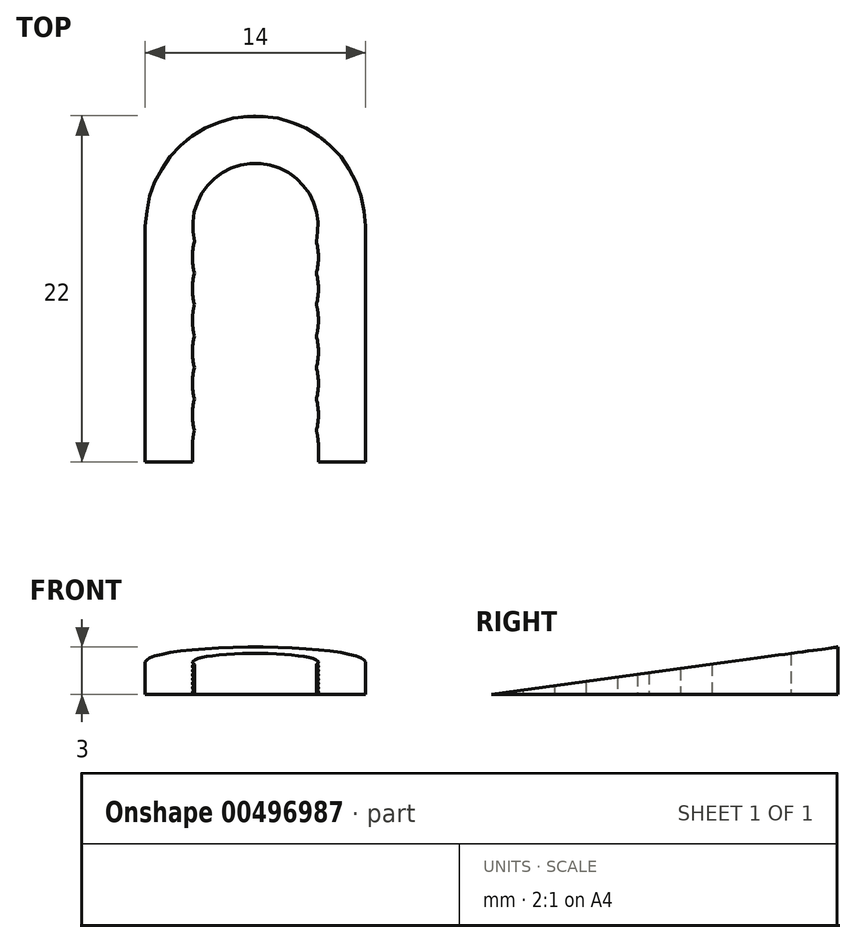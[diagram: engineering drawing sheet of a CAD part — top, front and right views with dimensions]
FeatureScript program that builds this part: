
annotation { "Feature Type Name" : "Feature", "Feature Type Description" : "" }
export const myFeature = defineFeature(function(context is Context, id is Id, definition is map)
    precondition{}
    {
        {
            var Q0;
            Q0=qCreatedBy(makeId("Top.planeOp"),FACE);
            var sketch = newSketch(context, id + "F0", { "sketchPlane" : qUnion([Q0])});
            skCircle(sketch, "E0", {"center": v(0, 0) * mm, "radius": 4 * mm});
            skCircle(sketch, "E1", {"center": v(0, 0) * mm, "radius": 7 * mm});
            skLineSegment(sketch, "E2.bottom", {"start": v(-7, 0) * mm, "end": v(7, 0) * mm});
            skLineSegment(sketch, "E2.top", {"start": v(-7, -15) * mm, "end": v(7, -15) * mm});
            skLineSegment(sketch, "E2.left", {"start": v(-7, 0) * mm, "end": v(-7, -15) * mm});
            skLineSegment(sketch, "E2.right", {"start": v(7, 0) * mm, "end": v(7, -15) * mm});
            skLineSegment(sketch, "E3.bottom", {"start": v(-4, 0) * mm, "end": v(4, 0) * mm});
            skLineSegment(sketch, "E3.top", {"start": v(-4, -15) * mm, "end": v(4, -15) * mm});
            skLineSegment(sketch, "E3.left", {"start": v(-4, 0) * mm, "end": v(-4, -15) * mm});
            skLineSegment(sketch, "E3.right", {"start": v(4, 0) * mm, "end": v(4, -15) * mm});
            skLineSegment(sketch, "E4", {"start": v(0, 0) * mm, "end": v(0, -15) * mm, "construction": true});
            skCircle(sketch, "E5.1.0.0", {"center": v(0, -2) * mm, "radius": 4 * mm});
            skCircle(sketch, "E5.2.0.0", {"center": v(0, -4) * mm, "radius": 4 * mm});
            skCircle(sketch, "E5.3.0.0", {"center": v(0, -6) * mm, "radius": 4 * mm});
            skCircle(sketch, "E5.4.0.0", {"center": v(0, -8) * mm, "radius": 4 * mm});
            skCircle(sketch, "E5.5.0.0", {"center": v(0, -10) * mm, "radius": 4 * mm});
            skCircle(sketch, "E5.6.0.0", {"center": v(0, -12) * mm, "radius": 4 * mm});
            skCircle(sketch, "E5.7.0.0", {"center": v(0, -14) * mm, "radius": 4 * mm});
            skLineSegment(sketch, "E5.direction1", {"start": v(0, 0) * mm, "end": v(0, -2) * mm, "construction": true});
            skSolve(sketch);
        }
        {
            var Q0;
            {var subQ4=sQuery(id+"F0.wireOp",EDGE,"E2.left");Q0=makeQuery(id+"F0.imprint","IMPRINT",FACE,{"disambiguationData":[TD([[makeQuery(id+"F0.imprint","IMPRINT",EDGE,{"derivedFrom":subQ4}),1.0]])]});}
            var Q1;
            {var subQ0=sQuery(id+"F0.wireOp",EDGE,"E3.left");var subQ1=makeQuery(id+"F0.imprint","INTERSECT",VERTEX,{"derivedFrom":[subQ0,sQuery(id+"F0.wireOp",EDGE,"E5.1.0.0")]});Q1=makeQuery(id+"F0.imprint","IMPRINT",FACE,{"disambiguationData":[TD([[makeQuery(id+"F0.imprint","IMPRINT",EDGE,{"disambiguationData":[TD([[subQ1,-1.0]])],"derivedFrom":subQ0}),-1.0]])]});}
            var Q2;
            {var subQ1=sQuery(id+"F0.wireOp",EDGE,"E2.bottom");var subQ5=sQuery(id+"F0.wireOp",EDGE,"E1");var subQ6=makeQuery(id+"F0.imprint","INTERSECT",VERTEX,{"derivedFrom":[subQ5,subQ1,sQuery(id+"F0.wireOp",EDGE,"E2.left")]});Q2=makeQuery(id+"F0.imprint","IMPRINT",FACE,{"disambiguationData":[TD([[makeQuery(id+"F0.imprint","IMPRINT",EDGE,{"disambiguationData":[TD([[subQ6,1.0]])],"derivedFrom":subQ5}),1.0]])]});}
            var Q3;
            {var subQ0=sQuery(id+"F0.wireOp",EDGE,"E3.right");var subQ1=makeQuery(id+"F0.imprint","INTERSECT",VERTEX,{"derivedFrom":[subQ0,sQuery(id+"F0.wireOp",EDGE,"E5.1.0.0")]});Q3=makeQuery(id+"F0.imprint","IMPRINT",FACE,{"disambiguationData":[TD([[makeQuery(id+"F0.imprint","IMPRINT",EDGE,{"disambiguationData":[TD([[subQ1,-1.0]])],"derivedFrom":subQ0}),1.0]])]});}
            var Q4;
            {var subQ4=sQuery(id+"F0.wireOp",EDGE,"E2.right");Q4=makeQuery(id+"F0.imprint","IMPRINT",FACE,{"disambiguationData":[TD([[makeQuery(id+"F0.imprint","IMPRINT",EDGE,{"derivedFrom":subQ4}),-1.0]])]});}
            var Q5;
            {var subQ1=sQuery(id+"F0.wireOp",EDGE,"E0");var subQ3=sQuery(id+"F0.wireOp",EDGE,"E5.1.0.0");var subQ4=makeQuery(id+"F0.imprint","INTERSECT",VERTEX,{"disambiguationData":[OD(0.0)],"derivedFrom":[subQ1,subQ3]});Q5=makeQuery(id+"F0.imprint","IMPRINT",FACE,{"disambiguationData":[TD([[makeQuery(id+"F0.imprint","IMPRINT",EDGE,{"disambiguationData":[TD([[subQ4,-1.0]])],"derivedFrom":subQ3}),-1.0]])]});}
            var Q6;
            {var subQ0=sQuery(id+"F0.wireOp",EDGE,"E5.1.0.0");var subQ1=sQuery(id+"F0.wireOp",EDGE,"E3.left");var subQ2=makeQuery(id+"F0.imprint","INTERSECT",VERTEX,{"derivedFrom":[subQ1,subQ0]});Q6=makeQuery(id+"F0.imprint","IMPRINT",FACE,{"disambiguationData":[TD([[makeQuery(id+"F0.imprint","IMPRINT",EDGE,{"disambiguationData":[TD([[subQ2,-1.0]])],"derivedFrom":subQ1}),1.0]])]});}
            var Q7;
            {var subQ0=sQuery(id+"F0.wireOp",EDGE,"E3.left");var subQ1=sQuery(id+"F0.wireOp",EDGE,"E1");var subQ2=makeQuery(id+"F0.imprint","INTERSECT",VERTEX,{"derivedFrom":[subQ1,subQ0]});Q7=makeQuery(id+"F0.imprint","IMPRINT",FACE,{"disambiguationData":[TD([[makeQuery(id+"F0.imprint","IMPRINT",EDGE,{"disambiguationData":[TD([[subQ2,-1.0]])],"derivedFrom":subQ1}),1.0]])]});}
            var Q8;
            {var subQ0=sQuery(id+"F0.wireOp",EDGE,"E5.3.0.0");var subQ1=sQuery(id+"F0.wireOp",EDGE,"E3.left");var subQ2=makeQuery(id+"F0.imprint","INTERSECT",VERTEX,{"derivedFrom":[subQ1,subQ0]});Q8=makeQuery(id+"F0.imprint","IMPRINT",FACE,{"disambiguationData":[TD([[makeQuery(id+"F0.imprint","IMPRINT",EDGE,{"disambiguationData":[TD([[subQ2,-1.0]])],"derivedFrom":subQ1}),1.0]])]});}
            var Q9;
            {var subQ0=sQuery(id+"F0.wireOp",EDGE,"E5.4.0.0");var subQ1=sQuery(id+"F0.wireOp",EDGE,"E3.left");var subQ2=makeQuery(id+"F0.imprint","INTERSECT",VERTEX,{"derivedFrom":[subQ1,subQ0]});Q9=makeQuery(id+"F0.imprint","IMPRINT",FACE,{"disambiguationData":[TD([[makeQuery(id+"F0.imprint","IMPRINT",EDGE,{"disambiguationData":[TD([[subQ2,-1.0]])],"derivedFrom":subQ1}),1.0]])]});}
            var Q10;
            {var subQ0=sQuery(id+"F0.wireOp",EDGE,"E5.5.0.0");var subQ1=sQuery(id+"F0.wireOp",EDGE,"E3.left");var subQ2=makeQuery(id+"F0.imprint","INTERSECT",VERTEX,{"derivedFrom":[subQ1,subQ0]});Q10=makeQuery(id+"F0.imprint","IMPRINT",FACE,{"disambiguationData":[TD([[makeQuery(id+"F0.imprint","IMPRINT",EDGE,{"disambiguationData":[TD([[subQ2,-1.0]])],"derivedFrom":subQ1}),1.0]])]});}
            var Q11;
            {var subQ0=sQuery(id+"F0.wireOp",EDGE,"E5.6.0.0");var subQ1=sQuery(id+"F0.wireOp",EDGE,"E3.left");var subQ2=makeQuery(id+"F0.imprint","INTERSECT",VERTEX,{"derivedFrom":[subQ1,subQ0]});Q11=makeQuery(id+"F0.imprint","IMPRINT",FACE,{"disambiguationData":[TD([[makeQuery(id+"F0.imprint","IMPRINT",EDGE,{"disambiguationData":[TD([[subQ2,-1.0]])],"derivedFrom":subQ1}),1.0]])]});}
            var Q12;
            {var subQ0=sQuery(id+"F0.wireOp",EDGE,"E5.6.0.0");var subQ1=sQuery(id+"F0.wireOp",EDGE,"E3.right");var subQ2=makeQuery(id+"F0.imprint","INTERSECT",VERTEX,{"derivedFrom":[subQ1,subQ0]});Q12=makeQuery(id+"F0.imprint","IMPRINT",FACE,{"disambiguationData":[TD([[makeQuery(id+"F0.imprint","IMPRINT",EDGE,{"disambiguationData":[TD([[subQ2,-1.0]])],"derivedFrom":subQ1}),-1.0]])]});}
            var Q13;
            {var subQ0=sQuery(id+"F0.wireOp",EDGE,"E5.5.0.0");var subQ1=sQuery(id+"F0.wireOp",EDGE,"E3.right");var subQ2=makeQuery(id+"F0.imprint","INTERSECT",VERTEX,{"derivedFrom":[subQ1,subQ0]});Q13=makeQuery(id+"F0.imprint","IMPRINT",FACE,{"disambiguationData":[TD([[makeQuery(id+"F0.imprint","IMPRINT",EDGE,{"disambiguationData":[TD([[subQ2,-1.0]])],"derivedFrom":subQ1}),-1.0]])]});}
            var Q14;
            {var subQ0=sQuery(id+"F0.wireOp",EDGE,"E5.4.0.0");var subQ1=sQuery(id+"F0.wireOp",EDGE,"E3.right");var subQ2=makeQuery(id+"F0.imprint","INTERSECT",VERTEX,{"derivedFrom":[subQ1,subQ0]});Q14=makeQuery(id+"F0.imprint","IMPRINT",FACE,{"disambiguationData":[TD([[makeQuery(id+"F0.imprint","IMPRINT",EDGE,{"disambiguationData":[TD([[subQ2,-1.0]])],"derivedFrom":subQ1}),-1.0]])]});}
            var Q15;
            {var subQ0=sQuery(id+"F0.wireOp",EDGE,"E5.3.0.0");var subQ1=sQuery(id+"F0.wireOp",EDGE,"E3.right");var subQ2=makeQuery(id+"F0.imprint","INTERSECT",VERTEX,{"derivedFrom":[subQ1,subQ0]});Q15=makeQuery(id+"F0.imprint","IMPRINT",FACE,{"disambiguationData":[TD([[makeQuery(id+"F0.imprint","IMPRINT",EDGE,{"disambiguationData":[TD([[subQ2,-1.0]])],"derivedFrom":subQ1}),-1.0]])]});}
            var Q16;
            {var subQ0=sQuery(id+"F0.wireOp",EDGE,"E5.3.0.0");var subQ1=sQuery(id+"F0.wireOp",EDGE,"E1");var subQ2=makeQuery(id+"F0.imprint","INTERSECT",VERTEX,{"disambiguationData":[OD(1.0)],"derivedFrom":[subQ1,subQ0]});Q16=makeQuery(id+"F0.imprint","IMPRINT",FACE,{"disambiguationData":[TD([[makeQuery(id+"F0.imprint","IMPRINT",EDGE,{"disambiguationData":[TD([[subQ2,-1.0]])],"derivedFrom":subQ1}),1.0]])]});}
            var Q17;
            {var subQ0=sQuery(id+"F0.wireOp",EDGE,"E5.1.0.0");var subQ1=sQuery(id+"F0.wireOp",EDGE,"E3.right");var subQ2=makeQuery(id+"F0.imprint","INTERSECT",VERTEX,{"derivedFrom":[subQ1,subQ0]});Q17=makeQuery(id+"F0.imprint","IMPRINT",FACE,{"disambiguationData":[TD([[makeQuery(id+"F0.imprint","IMPRINT",EDGE,{"disambiguationData":[TD([[subQ2,-1.0]])],"derivedFrom":subQ1}),-1.0]])]});}
            var Q18;
            {var subQ1=sQuery(id+"F0.wireOp",EDGE,"E0");var subQ3=sQuery(id+"F0.wireOp",EDGE,"E5.1.0.0");var subQ4=makeQuery(id+"F0.imprint","INTERSECT",VERTEX,{"disambiguationData":[OD(1.0)],"derivedFrom":[subQ1,subQ3]});Q18=makeQuery(id+"F0.imprint","IMPRINT",FACE,{"disambiguationData":[TD([[makeQuery(id+"F0.imprint","IMPRINT",EDGE,{"disambiguationData":[TD([[subQ4,1.0]])],"derivedFrom":subQ3}),-1.0]])]});}
            extrude(context, id + "F1", {"entities" : qUnion([Q0, Q1, Q2, Q3, Q4, Q5, Q6, Q7, Q8, Q9, Q10, Q11, Q12, Q13, Q14, Q15, Q16, Q17, Q18]), "depth" : 3 * mm});
        }
        {
            var Q0;
            Q0=qCreatedBy(makeId("Right.planeOp"),FACE);
            var sketch = newSketch(context, id + "F2", { "sketchPlane" : qUnion([Q0])});
            skLineSegment(sketch, "E6.0.0", {"start": v(-15, 0) * mm, "end": v(0, 0) * mm});
            skLineSegment(sketch, "E6.0.2", {"start": v(0, 3) * mm, "end": v(-15, 3) * mm});
            skLineSegment(sketch, "E6.0.3", {"start": v(-15, 3) * mm, "end": v(-15, 0) * mm});
            skLineSegment(sketch, "E7", {"start": v(7, 3) * mm, "end": v(7, 0) * mm});
            skLineSegment(sketch, "E8", {"start": v(7, 3) * mm, "end": v(-15, 0) * mm});
            skLineSegment(sketch, "E9", {"start": v(7, 3) * mm, "end": v(0, 3) * mm});
            skSolve(sketch);
        }
        {
            var Q0;
            Q0=makeQuery(id+"F2.imprint","IMPRINT",FACE,{"disambiguationData":[TD([[makeQuery(id+"F2.imprint","IMPRINT",EDGE,{"derivedFrom":sQuery(id+"F2.wireOp",EDGE,"E6.0.2")}),1.0]])]});
            extrude(context, id + "F3", {"entities" : qUnion([Q0]), "operationType" : NewBodyOperationType.REMOVE, "endBound" : BoundingType.SYMMETRIC, "depth" : 25 * mm});
        }
    });
